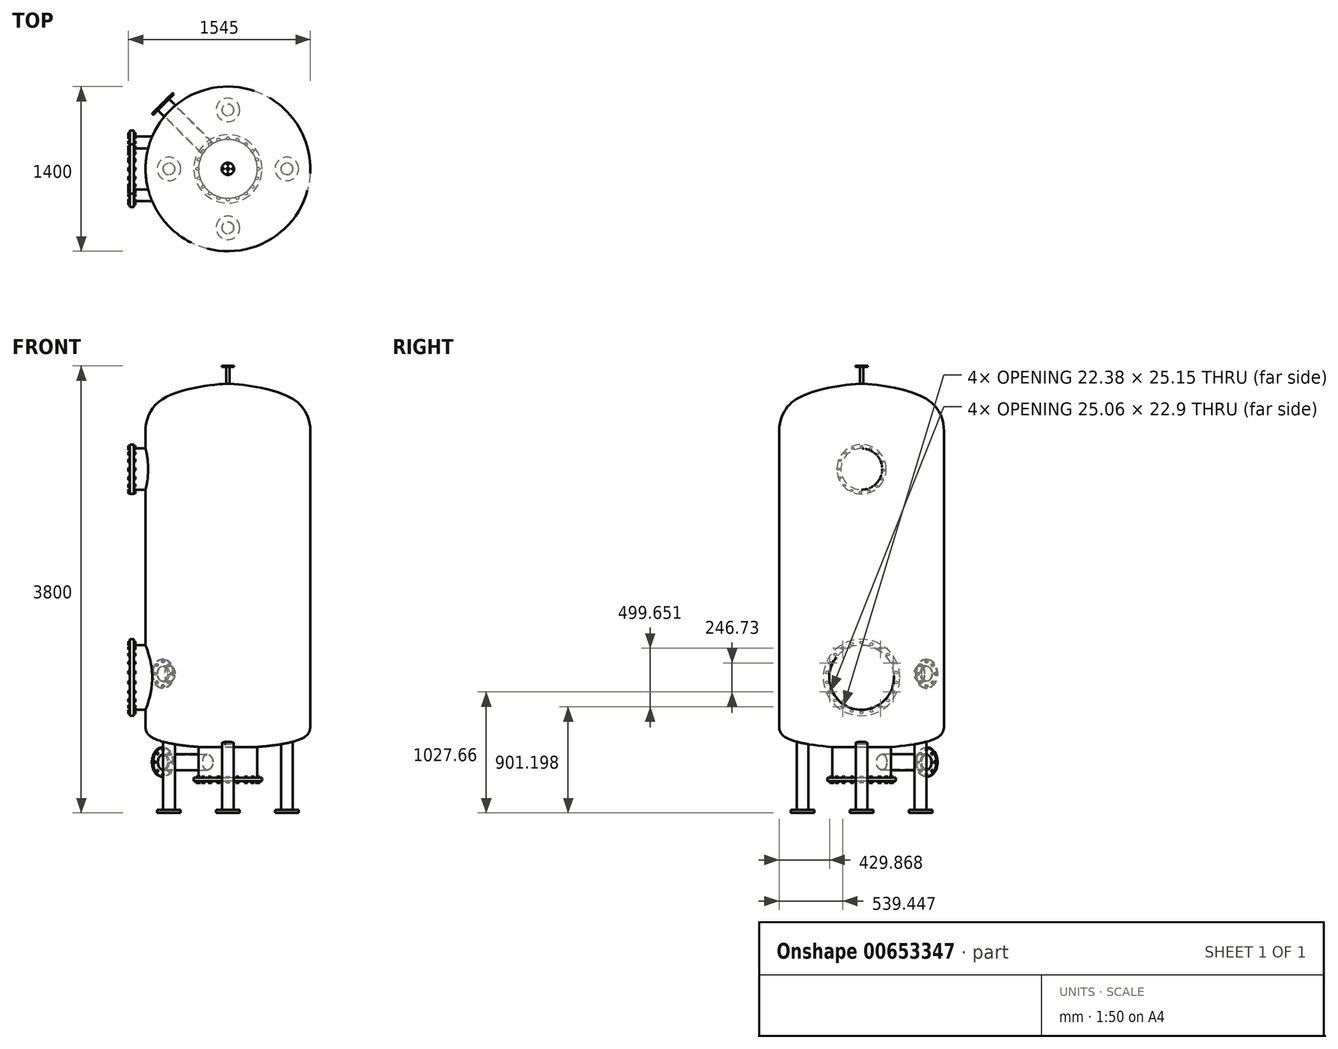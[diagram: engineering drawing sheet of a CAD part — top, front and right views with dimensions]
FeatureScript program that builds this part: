
annotation { "Feature Type Name" : "Feature", "Feature Type Description" : "" }
export const myFeature = defineFeature(function(context is Context, id is Id, definition is map)
    precondition{}
    {
        {
            var Q0;
            Q0=qCreatedBy(makeId("Front.planeOp"),FACE);
            var sketch = newSketch(context, id + "F0", { "sketchPlane" : qUnion([Q0])});
            skLineSegment(sketch, "E0.left", {"start": v(0, 0) * mm, "end": v(0, 3000) * mm});
            skLineSegment(sketch, "E0.right", {"start": v(700, 188.4) * mm, "end": v(700, 2700) * mm});
            skFitSpline(sketch, "E1", {"points": [v(700, 2700) * mm, v(561.33, 2963.36) * mm, v(0, 3098.34) * mm], "startDerivative": vector(-3.03, 549.76) * mm, "endDerivative": vector(-458.1, 7.94) * mm});
            skLineSegment(sketch, "E2", {"start": v(0, 3098.34) * mm, "end": v(0, 2986.2) * mm});
            skFitSpline(sketch, "E3", {"points": [v(0, 0) * mm, v(624.25, 80.53) * mm, v(700, 188.4) * mm], "startDerivative": vector(1247.83, 23.5) * mm, "endDerivative": vector(-2.18, 523.18) * mm});
            skSolve(sketch);
        }
        {
            var Q0;
            {var subQ1=sQuery(id+"F0.wireOp",EDGE,"E0.left");Q0=makeQuery(id+"F0.imprint","IMPRINT",FACE,{"disambiguationData":[TD([[makeQuery(id+"F0.imprint","IMPRINT",EDGE,{"derivedFrom":subQ1}),-1.0]])]});}
            var Q1;
            Q1=sQuery(id+"F0.wireOp",EDGE,"E0.left");
            revolve(context, id + "F1", {"entities" : qUnion([Q0]), "axis" : qUnion([Q1]), "revolveType" : RevolveType.FULL});
        }
        {
            var Q0;
            Q0=qCreatedBy(makeId("Top.planeOp"),FACE);
            cPlane(context, id + "F2", {"entities" : qUnion([Q0]), "cplaneType" : CPlaneType.OFFSET, "offset" : 150 * mm, "width" : 150 * mm, "height" : 150 * mm});
        }
        {
            var Q0;
            Q0=qCreatedBy(id+"F2.planeOp",FACE);
            var sketch = newSketch(context, id + "F3", { "sketchPlane" : qUnion([Q0])});
            skCircle(sketch, "E4", {"center": v(0, 0) * mm, "radius": 250 * mm});
            skSolve(sketch);
        }
        {
            var Q0;
            Q0 = qSketchRegion(id + "F3", true);
            extrude(context, id + "F4", {"entities" : qUnion([Q0]), "operationType" : NewBodyOperationType.ADD, "oppositeDirection" : true, "depth" : 400 * mm, "offsetDistance" : 25 * mm});
        }
        {
            var Q0;
            Q0=qCreatedBy(id+"F2.planeOp",FACE);
            var sketch = newSketch(context, id + "F5", { "sketchPlane" : qUnion([Q0])});
            skCircle(sketch, "E5", {"center": v(0, -500.95) * mm, "radius": 50 * mm});
            skCircle(sketch, "E6.1.0", {"center": v(500.95, 0) * mm, "radius": 50 * mm});
            skCircle(sketch, "E6.2.0", {"center": v(0, 500.95) * mm, "radius": 50 * mm});
            skCircle(sketch, "E6.3.0", {"center": v(-500.95, 0) * mm, "radius": 50 * mm});
            skPoint(sketch, "E6.center", {"position": v(0, 0) * mm});
            skSolve(sketch);
        }
        {
            var Q0;
            Q0 = qSketchRegion(id + "F5", true);
            extrude(context, id + "F6", {"entities" : qUnion([Q0]), "operationType" : NewBodyOperationType.ADD, "oppositeDirection" : true, "depth" : 700 * mm, "offsetDistance" : 25 * mm});
        }
        {
            var Q0;
            Q0=makeQuery(id+"F4.opExtrude","CAP_FACE",FACE,{"disambiguationData":[OSD([sQuery(id+"F3.wireOp",EDGE,"E4")])],"isStart":false});
            var sketch = newSketch(context, id + "F7", { "sketchPlane" : qUnion([Q0])});
            skCircle(sketch, "E7", {"center": v(0, 0) * mm, "radius": 290 * mm});
            skSolve(sketch);
        }
        {
            var Q0;
            Q0=makeQuery(id+"F7.imprint","IMPRINT",FACE,{"disambiguationData":[TD([[makeQuery(id+"F7.imprint","IMPRINT",EDGE,{"derivedFrom":sQuery(id+"F7.wireOp",EDGE,"E7")}),1.0]])]});
            var Q1;
            Q1=makeQuery(id+"F7.imprint","IMPRINT",FACE,{"disambiguationData":[TD([[makeQuery(id+"F7.imprint","IMPRINT",EDGE,{"derivedFrom":makeQuery(id+"F4.opExtrude","CAP_EDGE",EDGE,{"disambiguationData":[OSD([sQuery(id+"F3.wireOp",EDGE,"E4")])],"isStart":false})}),-1.0]])]});
            var Q2;
            Q2=sQuery(id+"F7.wireOp",EDGE,"E7");
            extrude(context, id + "F8", {"entities" : qUnion([Q0, Q1]), "operationType" : NewBodyOperationType.ADD, "surfaceEntities" : qUnion([Q2]), "depth" : 30 * mm, "offsetDistance" : 25 * mm});
        }
        {
            var Q0;
            Q0=makeQuery(id+"F8.opExtrude","CAP_FACE",FACE,{"disambiguationData":[OSD([sQuery(id+"F7.wireOp",EDGE,"E7")])],"isStart":false});
            var sketch = newSketch(context, id + "F9", { "sketchPlane" : qUnion([Q0])});
            skCircle(sketch, "E8.cCircle", {"center": v(260, 0) * mm, "radius": 12.3 * mm, "construction": true});
            skLineSegment(sketch, "E8.0", {"start": v(247.7, -7.1) * mm, "end": v(247.7, 7.1) * mm});
            skLineSegment(sketch, "E8.1", {"start": v(247.7, 7.1) * mm, "end": v(260, 14.2) * mm});
            skLineSegment(sketch, "E8.2", {"start": v(260, 14.2) * mm, "end": v(272.3, 7.1) * mm});
            skLineSegment(sketch, "E8.3", {"start": v(272.3, 7.1) * mm, "end": v(272.3, -7.1) * mm});
            skLineSegment(sketch, "E8.4", {"start": v(272.3, -7.1) * mm, "end": v(260, -14.2) * mm});
            skLineSegment(sketch, "E8.5", {"start": v(260, -14.2) * mm, "end": v(247.7, -7.1) * mm});
            skPoint(sketch, "E8.0.midPoint", {"position": v(247.7, 0) * mm});
            skLineSegment(sketch, "E9.1.0", {"start": v(242.89, 93.85) * mm, "end": v(256.78, 90.9) * mm});
            skLineSegment(sketch, "E9.1.1", {"start": v(261.17, 77.4) * mm, "end": v(251.66, 66.83) * mm});
            skLineSegment(sketch, "E9.1.2", {"start": v(251.66, 66.83) * mm, "end": v(237.77, 69.79) * mm});
            skPoint(sketch, "E9.1.3", {"position": v(235.58, 76.54) * mm});
            skCircle(sketch, "E9.1.4", {"center": v(247.27, 80.34) * mm, "radius": 12.3 * mm, "construction": true});
            skLineSegment(sketch, "E9.1.5", {"start": v(233.38, 83.3) * mm, "end": v(242.89, 93.85) * mm});
            skLineSegment(sketch, "E9.1.6", {"start": v(256.78, 90.9) * mm, "end": v(261.17, 77.4) * mm});
            skLineSegment(sketch, "E9.1.7", {"start": v(237.77, 69.79) * mm, "end": v(233.38, 83.3) * mm});
            skLineSegment(sketch, "E9.2.0", {"start": v(202, 164.32) * mm, "end": v(216.12, 165.8) * mm});
            skLineSegment(sketch, "E9.2.1", {"start": v(224.47, 154.3) * mm, "end": v(218.7, 141.33) * mm});
            skLineSegment(sketch, "E9.2.2", {"start": v(218.7, 141.33) * mm, "end": v(204.57, 139.85) * mm});
            skPoint(sketch, "E9.2.3", {"position": v(200.4, 145.6) * mm});
            skCircle(sketch, "E9.2.4", {"center": v(210.34, 152.82) * mm, "radius": 12.3 * mm, "construction": true});
            skLineSegment(sketch, "E9.2.5", {"start": v(196.22, 151.34) * mm, "end": v(202, 164.32) * mm});
            skLineSegment(sketch, "E9.2.6", {"start": v(216.12, 165.8) * mm, "end": v(224.47, 154.3) * mm});
            skLineSegment(sketch, "E9.2.7", {"start": v(204.57, 139.85) * mm, "end": v(196.22, 151.34) * mm});
            skLineSegment(sketch, "E9.3.0", {"start": v(141.33, 218.7) * mm, "end": v(154.3, 224.47) * mm});
            skLineSegment(sketch, "E9.3.1", {"start": v(165.8, 216.12) * mm, "end": v(164.32, 202) * mm});
            skLineSegment(sketch, "E9.3.2", {"start": v(164.32, 202) * mm, "end": v(151.34, 196.22) * mm});
            skPoint(sketch, "E9.3.3", {"position": v(145.6, 200.4) * mm});
            skCircle(sketch, "E9.3.4", {"center": v(152.82, 210.34) * mm, "radius": 12.3 * mm, "construction": true});
            skLineSegment(sketch, "E9.3.5", {"start": v(139.85, 204.57) * mm, "end": v(141.33, 218.7) * mm});
            skLineSegment(sketch, "E9.3.6", {"start": v(154.3, 224.47) * mm, "end": v(165.8, 216.12) * mm});
            skLineSegment(sketch, "E9.3.7", {"start": v(151.34, 196.22) * mm, "end": v(139.85, 204.57) * mm});
            skLineSegment(sketch, "E9.4.0", {"start": v(66.83, 251.66) * mm, "end": v(77.4, 261.17) * mm});
            skLineSegment(sketch, "E9.4.1", {"start": v(90.9, 256.78) * mm, "end": v(93.85, 242.89) * mm});
            skLineSegment(sketch, "E9.4.2", {"start": v(93.85, 242.89) * mm, "end": v(83.3, 233.38) * mm});
            skPoint(sketch, "E9.4.3", {"position": v(76.54, 235.58) * mm});
            skCircle(sketch, "E9.4.4", {"center": v(80.34, 247.27) * mm, "radius": 12.3 * mm, "construction": true});
            skLineSegment(sketch, "E9.4.5", {"start": v(69.79, 237.77) * mm, "end": v(66.83, 251.66) * mm});
            skLineSegment(sketch, "E9.4.6", {"start": v(77.4, 261.17) * mm, "end": v(90.9, 256.78) * mm});
            skLineSegment(sketch, "E9.4.7", {"start": v(83.3, 233.38) * mm, "end": v(69.79, 237.77) * mm});
            skLineSegment(sketch, "E9.5.0", {"start": v(-14.2, 260) * mm, "end": v(-7.1, 272.3) * mm});
            skLineSegment(sketch, "E9.5.1", {"start": v(7.1, 272.3) * mm, "end": v(14.2, 260) * mm});
            skLineSegment(sketch, "E9.5.2", {"start": v(14.2, 260) * mm, "end": v(7.1, 247.7) * mm});
            skPoint(sketch, "E9.5.3", {"position": v(0, 247.7) * mm});
            skCircle(sketch, "E9.5.4", {"center": v(0, 260) * mm, "radius": 12.3 * mm, "construction": true});
            skLineSegment(sketch, "E9.5.5", {"start": v(-7.1, 247.7) * mm, "end": v(-14.2, 260) * mm});
            skLineSegment(sketch, "E9.5.6", {"start": v(-7.1, 272.3) * mm, "end": v(7.1, 272.3) * mm});
            skLineSegment(sketch, "E9.5.7", {"start": v(7.1, 247.7) * mm, "end": v(-7.1, 247.7) * mm});
            skLineSegment(sketch, "E9.6.0", {"start": v(-93.85, 242.89) * mm, "end": v(-90.9, 256.78) * mm});
            skLineSegment(sketch, "E9.6.1", {"start": v(-77.4, 261.17) * mm, "end": v(-66.83, 251.66) * mm});
            skLineSegment(sketch, "E9.6.2", {"start": v(-66.83, 251.66) * mm, "end": v(-69.79, 237.77) * mm});
            skPoint(sketch, "E9.6.3", {"position": v(-76.54, 235.58) * mm});
            skCircle(sketch, "E9.6.4", {"center": v(-80.34, 247.27) * mm, "radius": 12.3 * mm, "construction": true});
            skLineSegment(sketch, "E9.6.5", {"start": v(-83.3, 233.38) * mm, "end": v(-93.85, 242.89) * mm});
            skLineSegment(sketch, "E9.6.6", {"start": v(-90.9, 256.78) * mm, "end": v(-77.4, 261.17) * mm});
            skLineSegment(sketch, "E9.6.7", {"start": v(-69.79, 237.77) * mm, "end": v(-83.3, 233.38) * mm});
            skLineSegment(sketch, "E9.7.0", {"start": v(-164.32, 202) * mm, "end": v(-165.8, 216.12) * mm});
            skLineSegment(sketch, "E9.7.1", {"start": v(-154.3, 224.47) * mm, "end": v(-141.33, 218.7) * mm});
            skLineSegment(sketch, "E9.7.2", {"start": v(-141.33, 218.7) * mm, "end": v(-139.85, 204.57) * mm});
            skPoint(sketch, "E9.7.3", {"position": v(-145.6, 200.4) * mm});
            skCircle(sketch, "E9.7.4", {"center": v(-152.82, 210.34) * mm, "radius": 12.3 * mm, "construction": true});
            skLineSegment(sketch, "E9.7.5", {"start": v(-151.34, 196.22) * mm, "end": v(-164.32, 202) * mm});
            skLineSegment(sketch, "E9.7.6", {"start": v(-165.8, 216.12) * mm, "end": v(-154.3, 224.47) * mm});
            skLineSegment(sketch, "E9.7.7", {"start": v(-139.85, 204.57) * mm, "end": v(-151.34, 196.22) * mm});
            skLineSegment(sketch, "E9.8.0", {"start": v(-218.7, 141.33) * mm, "end": v(-224.47, 154.3) * mm});
            skLineSegment(sketch, "E9.8.1", {"start": v(-216.12, 165.8) * mm, "end": v(-202, 164.32) * mm});
            skLineSegment(sketch, "E9.8.2", {"start": v(-202, 164.32) * mm, "end": v(-196.22, 151.34) * mm});
            skPoint(sketch, "E9.8.3", {"position": v(-200.4, 145.6) * mm});
            skCircle(sketch, "E9.8.4", {"center": v(-210.34, 152.82) * mm, "radius": 12.3 * mm, "construction": true});
            skLineSegment(sketch, "E9.8.5", {"start": v(-204.57, 139.85) * mm, "end": v(-218.7, 141.33) * mm});
            skLineSegment(sketch, "E9.8.6", {"start": v(-224.47, 154.3) * mm, "end": v(-216.12, 165.8) * mm});
            skLineSegment(sketch, "E9.8.7", {"start": v(-196.22, 151.34) * mm, "end": v(-204.57, 139.85) * mm});
            skLineSegment(sketch, "E9.9.0", {"start": v(-251.66, 66.83) * mm, "end": v(-261.17, 77.4) * mm});
            skLineSegment(sketch, "E9.9.1", {"start": v(-256.78, 90.9) * mm, "end": v(-242.89, 93.85) * mm});
            skLineSegment(sketch, "E9.9.2", {"start": v(-242.89, 93.85) * mm, "end": v(-233.38, 83.3) * mm});
            skPoint(sketch, "E9.9.3", {"position": v(-235.58, 76.54) * mm});
            skCircle(sketch, "E9.9.4", {"center": v(-247.27, 80.34) * mm, "radius": 12.3 * mm, "construction": true});
            skLineSegment(sketch, "E9.9.5", {"start": v(-237.77, 69.79) * mm, "end": v(-251.66, 66.83) * mm});
            skLineSegment(sketch, "E9.9.6", {"start": v(-261.17, 77.4) * mm, "end": v(-256.78, 90.9) * mm});
            skLineSegment(sketch, "E9.9.7", {"start": v(-233.38, 83.3) * mm, "end": v(-237.77, 69.79) * mm});
            skLineSegment(sketch, "E9.10.0", {"start": v(-260, -14.2) * mm, "end": v(-272.3, -7.1) * mm});
            skLineSegment(sketch, "E9.10.1", {"start": v(-272.3, 7.1) * mm, "end": v(-260, 14.2) * mm});
            skLineSegment(sketch, "E9.10.2", {"start": v(-260, 14.2) * mm, "end": v(-247.7, 7.1) * mm});
            skPoint(sketch, "E9.10.3", {"position": v(-247.7, 0) * mm});
            skCircle(sketch, "E9.10.4", {"center": v(-260, 0) * mm, "radius": 12.3 * mm, "construction": true});
            skLineSegment(sketch, "E9.10.5", {"start": v(-247.7, -7.1) * mm, "end": v(-260, -14.2) * mm});
            skLineSegment(sketch, "E9.10.6", {"start": v(-272.3, -7.1) * mm, "end": v(-272.3, 7.1) * mm});
            skLineSegment(sketch, "E9.10.7", {"start": v(-247.7, 7.1) * mm, "end": v(-247.7, -7.1) * mm});
            skLineSegment(sketch, "E9.11.0", {"start": v(-242.89, -93.85) * mm, "end": v(-256.78, -90.9) * mm});
            skLineSegment(sketch, "E9.11.1", {"start": v(-261.17, -77.4) * mm, "end": v(-251.66, -66.83) * mm});
            skLineSegment(sketch, "E9.11.2", {"start": v(-251.66, -66.83) * mm, "end": v(-237.77, -69.79) * mm});
            skPoint(sketch, "E9.11.3", {"position": v(-235.58, -76.54) * mm});
            skCircle(sketch, "E9.11.4", {"center": v(-247.27, -80.34) * mm, "radius": 12.3 * mm, "construction": true});
            skLineSegment(sketch, "E9.11.5", {"start": v(-233.38, -83.3) * mm, "end": v(-242.89, -93.85) * mm});
            skLineSegment(sketch, "E9.11.6", {"start": v(-256.78, -90.9) * mm, "end": v(-261.17, -77.4) * mm});
            skLineSegment(sketch, "E9.11.7", {"start": v(-237.77, -69.79) * mm, "end": v(-233.38, -83.3) * mm});
            skLineSegment(sketch, "E9.12.0", {"start": v(-202, -164.32) * mm, "end": v(-216.12, -165.8) * mm});
            skLineSegment(sketch, "E9.12.1", {"start": v(-224.47, -154.3) * mm, "end": v(-218.7, -141.33) * mm});
            skLineSegment(sketch, "E9.12.2", {"start": v(-218.7, -141.33) * mm, "end": v(-204.57, -139.85) * mm});
            skPoint(sketch, "E9.12.3", {"position": v(-200.4, -145.6) * mm});
            skCircle(sketch, "E9.12.4", {"center": v(-210.34, -152.82) * mm, "radius": 12.3 * mm, "construction": true});
            skLineSegment(sketch, "E9.12.5", {"start": v(-196.22, -151.34) * mm, "end": v(-202, -164.32) * mm});
            skLineSegment(sketch, "E9.12.6", {"start": v(-216.12, -165.8) * mm, "end": v(-224.47, -154.3) * mm});
            skLineSegment(sketch, "E9.12.7", {"start": v(-204.57, -139.85) * mm, "end": v(-196.22, -151.34) * mm});
            skLineSegment(sketch, "E9.13.0", {"start": v(-141.33, -218.7) * mm, "end": v(-154.3, -224.47) * mm});
            skLineSegment(sketch, "E9.13.1", {"start": v(-165.8, -216.12) * mm, "end": v(-164.32, -202) * mm});
            skLineSegment(sketch, "E9.13.2", {"start": v(-164.32, -202) * mm, "end": v(-151.34, -196.22) * mm});
            skPoint(sketch, "E9.13.3", {"position": v(-145.6, -200.4) * mm});
            skCircle(sketch, "E9.13.4", {"center": v(-152.82, -210.34) * mm, "radius": 12.3 * mm, "construction": true});
            skLineSegment(sketch, "E9.13.5", {"start": v(-139.85, -204.57) * mm, "end": v(-141.33, -218.7) * mm});
            skLineSegment(sketch, "E9.13.6", {"start": v(-154.3, -224.47) * mm, "end": v(-165.8, -216.12) * mm});
            skLineSegment(sketch, "E9.13.7", {"start": v(-151.34, -196.22) * mm, "end": v(-139.85, -204.57) * mm});
            skLineSegment(sketch, "E9.14.0", {"start": v(-66.83, -251.66) * mm, "end": v(-77.4, -261.17) * mm});
            skLineSegment(sketch, "E9.14.1", {"start": v(-90.9, -256.78) * mm, "end": v(-93.85, -242.89) * mm});
            skLineSegment(sketch, "E9.14.2", {"start": v(-93.85, -242.89) * mm, "end": v(-83.3, -233.38) * mm});
            skPoint(sketch, "E9.14.3", {"position": v(-76.54, -235.58) * mm});
            skCircle(sketch, "E9.14.4", {"center": v(-80.34, -247.27) * mm, "radius": 12.3 * mm, "construction": true});
            skLineSegment(sketch, "E9.14.5", {"start": v(-69.79, -237.77) * mm, "end": v(-66.83, -251.66) * mm});
            skLineSegment(sketch, "E9.14.6", {"start": v(-77.4, -261.17) * mm, "end": v(-90.9, -256.78) * mm});
            skLineSegment(sketch, "E9.14.7", {"start": v(-83.3, -233.38) * mm, "end": v(-69.79, -237.77) * mm});
            skLineSegment(sketch, "E9.15.0", {"start": v(14.2, -260) * mm, "end": v(7.1, -272.3) * mm});
            skLineSegment(sketch, "E9.15.1", {"start": v(-7.1, -272.3) * mm, "end": v(-14.2, -260) * mm});
            skLineSegment(sketch, "E9.15.2", {"start": v(-14.2, -260) * mm, "end": v(-7.1, -247.7) * mm});
            skPoint(sketch, "E9.15.3", {"position": v(0, -247.7) * mm});
            skCircle(sketch, "E9.15.4", {"center": v(0, -260) * mm, "radius": 12.3 * mm, "construction": true});
            skLineSegment(sketch, "E9.15.5", {"start": v(7.1, -247.7) * mm, "end": v(14.2, -260) * mm});
            skLineSegment(sketch, "E9.15.6", {"start": v(7.1, -272.3) * mm, "end": v(-7.1, -272.3) * mm});
            skLineSegment(sketch, "E9.15.7", {"start": v(-7.1, -247.7) * mm, "end": v(7.1, -247.7) * mm});
            skLineSegment(sketch, "E9.16.0", {"start": v(93.85, -242.89) * mm, "end": v(90.9, -256.78) * mm});
            skLineSegment(sketch, "E9.16.1", {"start": v(77.4, -261.17) * mm, "end": v(66.83, -251.66) * mm});
            skLineSegment(sketch, "E9.16.2", {"start": v(66.83, -251.66) * mm, "end": v(69.79, -237.77) * mm});
            skPoint(sketch, "E9.16.3", {"position": v(76.54, -235.58) * mm});
            skCircle(sketch, "E9.16.4", {"center": v(80.34, -247.27) * mm, "radius": 12.3 * mm, "construction": true});
            skLineSegment(sketch, "E9.16.5", {"start": v(83.3, -233.38) * mm, "end": v(93.85, -242.89) * mm});
            skLineSegment(sketch, "E9.16.6", {"start": v(90.9, -256.78) * mm, "end": v(77.4, -261.17) * mm});
            skLineSegment(sketch, "E9.16.7", {"start": v(69.79, -237.77) * mm, "end": v(83.3, -233.38) * mm});
            skLineSegment(sketch, "E9.17.0", {"start": v(164.32, -202) * mm, "end": v(165.8, -216.12) * mm});
            skLineSegment(sketch, "E9.17.1", {"start": v(154.3, -224.47) * mm, "end": v(141.33, -218.7) * mm});
            skLineSegment(sketch, "E9.17.2", {"start": v(141.33, -218.7) * mm, "end": v(139.85, -204.57) * mm});
            skPoint(sketch, "E9.17.3", {"position": v(145.6, -200.4) * mm});
            skCircle(sketch, "E9.17.4", {"center": v(152.82, -210.34) * mm, "radius": 12.3 * mm, "construction": true});
            skLineSegment(sketch, "E9.17.5", {"start": v(151.34, -196.22) * mm, "end": v(164.32, -202) * mm});
            skLineSegment(sketch, "E9.17.6", {"start": v(165.8, -216.12) * mm, "end": v(154.3, -224.47) * mm});
            skLineSegment(sketch, "E9.17.7", {"start": v(139.85, -204.57) * mm, "end": v(151.34, -196.22) * mm});
            skLineSegment(sketch, "E9.18.0", {"start": v(218.7, -141.33) * mm, "end": v(224.47, -154.3) * mm});
            skLineSegment(sketch, "E9.18.1", {"start": v(216.12, -165.8) * mm, "end": v(202, -164.32) * mm});
            skLineSegment(sketch, "E9.18.2", {"start": v(202, -164.32) * mm, "end": v(196.22, -151.34) * mm});
            skPoint(sketch, "E9.18.3", {"position": v(200.4, -145.6) * mm});
            skCircle(sketch, "E9.18.4", {"center": v(210.34, -152.82) * mm, "radius": 12.3 * mm, "construction": true});
            skLineSegment(sketch, "E9.18.5", {"start": v(204.57, -139.85) * mm, "end": v(218.7, -141.33) * mm});
            skLineSegment(sketch, "E9.18.6", {"start": v(224.47, -154.3) * mm, "end": v(216.12, -165.8) * mm});
            skLineSegment(sketch, "E9.18.7", {"start": v(196.22, -151.34) * mm, "end": v(204.57, -139.85) * mm});
            skLineSegment(sketch, "E9.19.0", {"start": v(251.66, -66.83) * mm, "end": v(261.17, -77.4) * mm});
            skLineSegment(sketch, "E9.19.1", {"start": v(256.78, -90.9) * mm, "end": v(242.89, -93.85) * mm});
            skLineSegment(sketch, "E9.19.2", {"start": v(242.89, -93.85) * mm, "end": v(233.38, -83.3) * mm});
            skPoint(sketch, "E9.19.3", {"position": v(235.58, -76.54) * mm});
            skCircle(sketch, "E9.19.4", {"center": v(247.27, -80.34) * mm, "radius": 12.3 * mm, "construction": true});
            skLineSegment(sketch, "E9.19.5", {"start": v(237.77, -69.79) * mm, "end": v(251.66, -66.83) * mm});
            skLineSegment(sketch, "E9.19.6", {"start": v(261.17, -77.4) * mm, "end": v(256.78, -90.9) * mm});
            skLineSegment(sketch, "E9.19.7", {"start": v(233.38, -83.3) * mm, "end": v(237.77, -69.79) * mm});
            skPoint(sketch, "E9.center", {"position": v(0, 0) * mm});
            skSolve(sketch);
        }
        {
            var Q0;
            Q0 = qSketchRegion(id + "F9", true);
            extrude(context, id + "F10", {"entities" : qUnion([Q0]), "operationType" : NewBodyOperationType.ADD, "depth" : 15 * mm, "offsetDistance" : 25 * mm, "hasSecondDirection" : true, "secondDirectionOppositeDirection" : true, "secondDirectionDepth" : 40 * mm});
        }
        {
            var Q0;
            Q0=makeQuery(id+"F6.opExtrude","CAP_FACE",FACE,{"disambiguationData":[OSD([sQuery(id+"F5.wireOp",EDGE,"E6.2.0")])],"isStart":false});
            var sketch = newSketch(context, id + "F11", { "sketchPlane" : qUnion([Q0])});
            skCircle(sketch, "E10", {"center": v(0, -500.95) * mm, "radius": 100 * mm});
            skCircle(sketch, "E11.1.0", {"center": v(500.95, 0) * mm, "radius": 100 * mm});
            skCircle(sketch, "E11.2.0", {"center": v(0, 500.95) * mm, "radius": 100 * mm});
            skCircle(sketch, "E11.3.0", {"center": v(-500.95, 0) * mm, "radius": 100 * mm});
            skPoint(sketch, "E11.center", {"position": v(0, 0) * mm});
            skSolve(sketch);
        }
        {
            var Q0;
            Q0 = qSketchRegion(id + "F11", true);
            extrude(context, id + "F12", {"entities" : qUnion([Q0]), "operationType" : NewBodyOperationType.ADD, "oppositeDirection" : true, "depth" : 25 * mm, "offsetDistance" : 25 * mm});
        }
        {
            var Q0;
            Q0=makeQuery(id+"F8.opExtrude","CAP_FACE",FACE,{"disambiguationData":[OSD([sQuery(id+"F7.wireOp",EDGE,"E7")])],"isStart":false});
            var sketch = newSketch(context, id + "F13", { "sketchPlane" : qUnion([Q0])});
            skLineSegment(sketch, "E12", {"start": v(0, 0) * mm, "end": v(-124.4, -124.4) * mm});
            skLineSegment(sketch, "E13", {"start": v(0, 0) * mm, "end": v(-110.44, 0) * mm});
            skSolve(sketch);
        }
        {
            var Q0;
            Q0=sQuery(id+"F13.wireOp",EDGE,"E12");
            cPlane(context, id + "F14", {"entities" : qUnion([Q0]), "cplaneType" : CPlaneType.MID_PLANE, "offset" : 25 * mm, "width" : 150 * mm, "height" : 150 * mm});
        }
        {
            var Q0;
            Q0=qCreatedBy(id+"F14.planeOp",FACE);
            var sketch = newSketch(context, id + "F15", { "sketchPlane" : qUnion([Q0])});
            skCircle(sketch, "E14", {"center": v(0, -118.9) * mm, "radius": 67.5 * mm});
            skCircle(sketch, "E15", {"center": v(0, -118.9) * mm, "radius": 62.5 * mm});
            skSolve(sketch);
        }
        {
            var Q0;
            Q0 = qSketchRegion(id + "F15", true);
            extrude(context, id + "F16", {"entities" : qUnion([Q0]), "operationType" : NewBodyOperationType.ADD, "depth" : 700 * mm, "offsetDistance" : 25 * mm});
        }
        {
            var Q0;
            Q0=makeQuery(id+"F16.opExtrude","CAP_FACE",FACE,{"disambiguationData":[OSD([sQuery(id+"F15.wireOp",EDGE,"E14"),sQuery(id+"F15.wireOp",EDGE,"E15")])],"isStart":false});
            var sketch = newSketch(context, id + "F17", { "sketchPlane" : qUnion([Q0])});
            skCircle(sketch, "E16", {"center": v(0, -118.9) * mm, "radius": 125 * mm});
            skCircle(sketch, "E17", {"center": v(0, -13.9) * mm, "radius": 9 * mm});
            skCircle(sketch, "E18.1.0", {"center": v(-74.25, -44.65) * mm, "radius": 9 * mm});
            skCircle(sketch, "E18.2.0", {"center": v(-105, -118.9) * mm, "radius": 9 * mm});
            skCircle(sketch, "E18.3.0", {"center": v(-74.25, -193.14) * mm, "radius": 9 * mm});
            skCircle(sketch, "E18.4.0", {"center": v(0, -223.9) * mm, "radius": 9 * mm});
            skCircle(sketch, "E18.5.0", {"center": v(74.25, -193.14) * mm, "radius": 9 * mm});
            skCircle(sketch, "E18.6.0", {"center": v(105, -118.9) * mm, "radius": 9 * mm});
            skCircle(sketch, "E18.7.0", {"center": v(74.25, -44.65) * mm, "radius": 9 * mm});
            skSolve(sketch);
        }
        {
            var Q0;
            Q0=makeQuery(id+"F17.imprint","IMPRINT",FACE,{"disambiguationData":[TD([[makeQuery(id+"F17.imprint","IMPRINT",EDGE,{"derivedFrom":sQuery(id+"F17.wireOp",EDGE,"E16")}),1.0]])]});
            extrude(context, id + "F18", {"entities" : qUnion([Q0]), "operationType" : NewBodyOperationType.ADD, "oppositeDirection" : true, "depth" : 15 * mm, "offsetDistance" : 25 * mm});
        }
        {
            var Q0;
            Q0=qCreatedBy(makeId("Right.planeOp"),FACE);
            var sketch = newSketch(context, id + "F19", { "sketchPlane" : qUnion([Q0])});
            skCircle(sketch, "E19", {"center": v(0, 2372.8) * mm, "radius": 175 * mm});
            skCircle(sketch, "E20", {"center": v(0, 601.02) * mm, "radius": 275 * mm});
            skSolve(sketch);
        }
        {
            var Q0;
            Q0 = qSketchRegion(id + "F19", true);
            extrude(context, id + "F20", {"entities" : qUnion([Q0]), "operationType" : NewBodyOperationType.ADD, "oppositeDirection" : true, "depth" : 800 * mm, "offsetDistance" : 25 * mm});
        }
        {
            var Q0;
            Q0=makeQuery(id+"F20.opExtrude","CAP_FACE",FACE,{"disambiguationData":[OSD([sQuery(id+"F19.wireOp",EDGE,"E20")])],"isStart":false});
            var sketch = newSketch(context, id + "F21", { "sketchPlane" : qUnion([Q0])});
            skCircle(sketch, "E21", {"center": v(0, 601.02) * mm, "radius": 325 * mm});
            skCircle(sketch, "E22", {"center": v(0, 2372.16) * mm, "radius": 210 * mm});
            skSolve(sketch);
        }
        {
            var Q0;
            Q0 = qSketchRegion(id + "F21", true);
            extrude(context, id + "F22", {"entities" : qUnion([Q0]), "operationType" : NewBodyOperationType.ADD, "depth" : 35 * mm, "offsetDistance" : 25 * mm});
        }
        {
            var Q0;
            Q0=makeQuery(id+"F22.opExtrude","CAP_FACE",FACE,{"disambiguationData":[OSD([sQuery(id+"F21.wireOp",EDGE,"E21")])],"isStart":false});
            var sketch = newSketch(context, id + "F23", { "sketchPlane" : qUnion([Q0])});
            skCircle(sketch, "E23.cCircle", {"center": v(0, 898) * mm, "radius": 10.9 * mm, "construction": true});
            skLineSegment(sketch, "E23.0", {"start": v(6.3, 887.09) * mm, "end": v(-6.3, 887.09) * mm});
            skLineSegment(sketch, "E23.1", {"start": v(-6.3, 887.09) * mm, "end": v(-12.59, 898) * mm});
            skLineSegment(sketch, "E23.2", {"start": v(-12.59, 898) * mm, "end": v(-6.3, 908.9) * mm});
            skLineSegment(sketch, "E23.3", {"start": v(-6.3, 908.9) * mm, "end": v(6.3, 908.9) * mm});
            skLineSegment(sketch, "E23.4", {"start": v(6.3, 908.9) * mm, "end": v(12.59, 898) * mm});
            skLineSegment(sketch, "E23.5", {"start": v(12.59, 898) * mm, "end": v(6.3, 887.09) * mm});
            skPoint(sketch, "E23.0.midPoint", {"position": v(0, 887.09) * mm});
            skLineSegment(sketch, "E24.1.0", {"start": v(-86.63, 873.73) * mm, "end": v(-95.75, 882.42) * mm});
            skCircle(sketch, "E24.1.1", {"center": v(-83.67, 885.96) * mm, "radius": 10.9 * mm, "construction": true});
            skPoint(sketch, "E24.1.2", {"position": v(-80.6, 875.5) * mm});
            skLineSegment(sketch, "E24.1.3", {"start": v(-71.59, 889.5) * mm, "end": v(-74.55, 877.28) * mm});
            skLineSegment(sketch, "E24.1.4", {"start": v(-92.78, 894.65) * mm, "end": v(-80.7, 898.2) * mm});
            skLineSegment(sketch, "E24.1.5", {"start": v(-74.55, 877.28) * mm, "end": v(-86.63, 873.73) * mm});
            skLineSegment(sketch, "E24.1.6", {"start": v(-80.7, 898.2) * mm, "end": v(-71.59, 889.5) * mm});
            skLineSegment(sketch, "E24.1.7", {"start": v(-95.75, 882.42) * mm, "end": v(-92.78, 894.65) * mm});
            skLineSegment(sketch, "E24.2.0", {"start": v(-159.95, 838.27) * mm, "end": v(-171.14, 844.04) * mm});
            skCircle(sketch, "E24.2.1", {"center": v(-160.55, 850.85) * mm, "radius": 10.9 * mm, "construction": true});
            skPoint(sketch, "E24.2.2", {"position": v(-154.66, 841.68) * mm});
            skLineSegment(sketch, "E24.2.3", {"start": v(-149.96, 857.66) * mm, "end": v(-149.36, 845.08) * mm});
            skLineSegment(sketch, "E24.2.4", {"start": v(-171.74, 856.62) * mm, "end": v(-161.15, 863.42) * mm});
            skLineSegment(sketch, "E24.2.5", {"start": v(-149.36, 845.08) * mm, "end": v(-159.95, 838.27) * mm});
            skLineSegment(sketch, "E24.2.6", {"start": v(-161.15, 863.42) * mm, "end": v(-149.96, 857.66) * mm});
            skLineSegment(sketch, "E24.2.7", {"start": v(-171.14, 844.04) * mm, "end": v(-171.74, 856.62) * mm});
            skLineSegment(sketch, "E24.3.0", {"start": v(-220.32, 783.6) * mm, "end": v(-232.68, 785.98) * mm});
            skCircle(sketch, "E24.3.1", {"center": v(-224.43, 795.5) * mm, "radius": 10.9 * mm, "construction": true});
            skPoint(sketch, "E24.3.2", {"position": v(-216.2, 788.36) * mm});
            skLineSegment(sketch, "E24.3.3", {"start": v(-216.19, 805.01) * mm, "end": v(-212.07, 793.11) * mm});
            skLineSegment(sketch, "E24.3.4", {"start": v(-236.8, 797.88) * mm, "end": v(-228.55, 807.4) * mm});
            skLineSegment(sketch, "E24.3.5", {"start": v(-212.07, 793.11) * mm, "end": v(-220.32, 783.6) * mm});
            skLineSegment(sketch, "E24.3.6", {"start": v(-228.55, 807.4) * mm, "end": v(-216.19, 805.01) * mm});
            skLineSegment(sketch, "E24.3.7", {"start": v(-232.68, 785.98) * mm, "end": v(-236.8, 797.88) * mm});
            skLineSegment(sketch, "E24.4.0", {"start": v(-262.83, 714.13) * mm, "end": v(-275.36, 712.94) * mm});
            skCircle(sketch, "E24.4.1", {"center": v(-270.13, 724.39) * mm, "radius": 10.9 * mm, "construction": true});
            skPoint(sketch, "E24.4.2", {"position": v(-260.21, 719.86) * mm});
            skLineSegment(sketch, "E24.4.3", {"start": v(-264.9, 735.84) * mm, "end": v(-257.6, 725.59) * mm});
            skLineSegment(sketch, "E24.4.4", {"start": v(-282.66, 723.2) * mm, "end": v(-277.43, 734.64) * mm});
            skLineSegment(sketch, "E24.4.5", {"start": v(-257.6, 725.59) * mm, "end": v(-262.83, 714.13) * mm});
            skLineSegment(sketch, "E24.4.6", {"start": v(-277.43, 734.64) * mm, "end": v(-264.9, 735.84) * mm});
            skLineSegment(sketch, "E24.4.7", {"start": v(-275.36, 712.94) * mm, "end": v(-282.66, 723.2) * mm});
            skLineSegment(sketch, "E24.5.0", {"start": v(-284.05, 635.5) * mm, "end": v(-295.74, 630.83) * mm});
            skCircle(sketch, "E24.5.1", {"center": v(-293.95, 643.29) * mm, "radius": 10.9 * mm, "construction": true});
            skPoint(sketch, "E24.5.2", {"position": v(-283.15, 641.74) * mm});
            skLineSegment(sketch, "E24.5.3", {"start": v(-292.15, 655.75) * mm, "end": v(-282.26, 647.97) * mm});
            skLineSegment(sketch, "E24.5.4", {"start": v(-305.63, 638.6) * mm, "end": v(-303.84, 651.07) * mm});
            skLineSegment(sketch, "E24.5.5", {"start": v(-282.26, 647.97) * mm, "end": v(-284.05, 635.5) * mm});
            skLineSegment(sketch, "E24.5.6", {"start": v(-303.84, 651.07) * mm, "end": v(-292.15, 655.75) * mm});
            skLineSegment(sketch, "E24.5.7", {"start": v(-295.74, 630.83) * mm, "end": v(-305.63, 638.6) * mm});
            skLineSegment(sketch, "E24.6.0", {"start": v(-282.26, 554.08) * mm, "end": v(-292.15, 546.3) * mm});
            skCircle(sketch, "E24.6.1", {"center": v(-293.95, 558.76) * mm, "radius": 10.9 * mm, "construction": true});
            skPoint(sketch, "E24.6.2", {"position": v(-283.15, 560.31) * mm});
            skLineSegment(sketch, "E24.6.3", {"start": v(-295.74, 571.22) * mm, "end": v(-284.05, 566.54) * mm});
            skLineSegment(sketch, "E24.6.4", {"start": v(-303.84, 550.98) * mm, "end": v(-305.63, 563.44) * mm});
            skLineSegment(sketch, "E24.6.5", {"start": v(-284.05, 566.54) * mm, "end": v(-282.26, 554.08) * mm});
            skLineSegment(sketch, "E24.6.6", {"start": v(-305.63, 563.44) * mm, "end": v(-295.74, 571.22) * mm});
            skLineSegment(sketch, "E24.6.7", {"start": v(-292.15, 546.3) * mm, "end": v(-303.84, 550.98) * mm});
            skLineSegment(sketch, "E24.7.0", {"start": v(-257.6, 476.46) * mm, "end": v(-264.9, 466.2) * mm});
            skCircle(sketch, "E24.7.1", {"center": v(-270.13, 477.66) * mm, "radius": 10.9 * mm, "construction": true});
            skPoint(sketch, "E24.7.2", {"position": v(-260.21, 482.19) * mm});
            skLineSegment(sketch, "E24.7.3", {"start": v(-275.36, 489.11) * mm, "end": v(-262.83, 487.91) * mm});
            skLineSegment(sketch, "E24.7.4", {"start": v(-277.43, 467.4) * mm, "end": v(-282.66, 478.86) * mm});
            skLineSegment(sketch, "E24.7.5", {"start": v(-262.83, 487.91) * mm, "end": v(-257.6, 476.46) * mm});
            skLineSegment(sketch, "E24.7.6", {"start": v(-282.66, 478.86) * mm, "end": v(-275.36, 489.11) * mm});
            skLineSegment(sketch, "E24.7.7", {"start": v(-264.9, 466.2) * mm, "end": v(-277.43, 467.4) * mm});
            skLineSegment(sketch, "E24.8.0", {"start": v(-212.07, 408.93) * mm, "end": v(-216.19, 397.04) * mm});
            skCircle(sketch, "E24.8.1", {"center": v(-224.43, 406.55) * mm, "radius": 10.9 * mm, "construction": true});
            skPoint(sketch, "E24.8.2", {"position": v(-216.2, 413.7) * mm});
            skLineSegment(sketch, "E24.8.3", {"start": v(-232.68, 416.07) * mm, "end": v(-220.32, 418.45) * mm});
            skLineSegment(sketch, "E24.8.4", {"start": v(-228.55, 394.65) * mm, "end": v(-236.8, 404.17) * mm});
            skLineSegment(sketch, "E24.8.5", {"start": v(-220.32, 418.45) * mm, "end": v(-212.07, 408.93) * mm});
            skLineSegment(sketch, "E24.8.6", {"start": v(-236.8, 404.17) * mm, "end": v(-232.68, 416.07) * mm});
            skLineSegment(sketch, "E24.8.7", {"start": v(-216.19, 397.04) * mm, "end": v(-228.55, 394.65) * mm});
            skLineSegment(sketch, "E24.9.0", {"start": v(-149.36, 356.97) * mm, "end": v(-149.96, 344.4) * mm});
            skCircle(sketch, "E24.9.1", {"center": v(-160.55, 351.2) * mm, "radius": 10.9 * mm, "construction": true});
            skPoint(sketch, "E24.9.2", {"position": v(-154.66, 360.37) * mm});
            skLineSegment(sketch, "E24.9.3", {"start": v(-171.14, 358) * mm, "end": v(-159.95, 363.77) * mm});
            skLineSegment(sketch, "E24.9.4", {"start": v(-161.15, 338.62) * mm, "end": v(-171.74, 345.43) * mm});
            skLineSegment(sketch, "E24.9.5", {"start": v(-159.95, 363.77) * mm, "end": v(-149.36, 356.97) * mm});
            skLineSegment(sketch, "E24.9.6", {"start": v(-171.74, 345.43) * mm, "end": v(-171.14, 358) * mm});
            skLineSegment(sketch, "E24.9.7", {"start": v(-149.96, 344.4) * mm, "end": v(-161.15, 338.62) * mm});
            skLineSegment(sketch, "E24.10.0", {"start": v(-74.55, 324.77) * mm, "end": v(-71.59, 312.54) * mm});
            skCircle(sketch, "E24.10.1", {"center": v(-83.67, 316.08) * mm, "radius": 10.9 * mm, "construction": true});
            skPoint(sketch, "E24.10.2", {"position": v(-80.6, 326.55) * mm});
            skLineSegment(sketch, "E24.10.3", {"start": v(-95.75, 319.63) * mm, "end": v(-86.63, 328.32) * mm});
            skLineSegment(sketch, "E24.10.4", {"start": v(-80.7, 303.85) * mm, "end": v(-92.78, 307.4) * mm});
            skLineSegment(sketch, "E24.10.5", {"start": v(-86.63, 328.32) * mm, "end": v(-74.55, 324.77) * mm});
            skLineSegment(sketch, "E24.10.6", {"start": v(-92.78, 307.4) * mm, "end": v(-95.75, 319.63) * mm});
            skLineSegment(sketch, "E24.10.7", {"start": v(-71.59, 312.54) * mm, "end": v(-80.7, 303.85) * mm});
            skLineSegment(sketch, "E24.11.0", {"start": v(6.3, 314.96) * mm, "end": v(12.59, 304.06) * mm});
            skCircle(sketch, "E24.11.1", {"center": v(0, 304.06) * mm, "radius": 10.9 * mm, "construction": true});
            skPoint(sketch, "E24.11.2", {"position": v(0, 314.96) * mm});
            skLineSegment(sketch, "E24.11.3", {"start": v(-12.59, 304.06) * mm, "end": v(-6.3, 314.96) * mm});
            skLineSegment(sketch, "E24.11.4", {"start": v(6.3, 293.15) * mm, "end": v(-6.3, 293.15) * mm});
            skLineSegment(sketch, "E24.11.5", {"start": v(-6.3, 314.96) * mm, "end": v(6.3, 314.96) * mm});
            skLineSegment(sketch, "E24.11.6", {"start": v(-6.3, 293.15) * mm, "end": v(-12.59, 304.06) * mm});
            skLineSegment(sketch, "E24.11.7", {"start": v(12.59, 304.06) * mm, "end": v(6.3, 293.15) * mm});
            skLineSegment(sketch, "E24.12.0", {"start": v(86.63, 328.32) * mm, "end": v(95.75, 319.63) * mm});
            skCircle(sketch, "E24.12.1", {"center": v(83.67, 316.08) * mm, "radius": 10.9 * mm, "construction": true});
            skPoint(sketch, "E24.12.2", {"position": v(80.6, 326.55) * mm});
            skLineSegment(sketch, "E24.12.3", {"start": v(71.59, 312.54) * mm, "end": v(74.55, 324.77) * mm});
            skLineSegment(sketch, "E24.12.4", {"start": v(92.78, 307.4) * mm, "end": v(80.7, 303.85) * mm});
            skLineSegment(sketch, "E24.12.5", {"start": v(74.55, 324.77) * mm, "end": v(86.63, 328.32) * mm});
            skLineSegment(sketch, "E24.12.6", {"start": v(80.7, 303.85) * mm, "end": v(71.59, 312.54) * mm});
            skLineSegment(sketch, "E24.12.7", {"start": v(95.75, 319.63) * mm, "end": v(92.78, 307.4) * mm});
            skLineSegment(sketch, "E24.13.0", {"start": v(159.95, 363.77) * mm, "end": v(171.14, 358) * mm});
            skCircle(sketch, "E24.13.1", {"center": v(160.55, 351.2) * mm, "radius": 10.9 * mm, "construction": true});
            skPoint(sketch, "E24.13.2", {"position": v(154.66, 360.37) * mm});
            skLineSegment(sketch, "E24.13.3", {"start": v(149.96, 344.4) * mm, "end": v(149.36, 356.97) * mm});
            skLineSegment(sketch, "E24.13.4", {"start": v(171.74, 345.43) * mm, "end": v(161.15, 338.62) * mm});
            skLineSegment(sketch, "E24.13.5", {"start": v(149.36, 356.97) * mm, "end": v(159.95, 363.77) * mm});
            skLineSegment(sketch, "E24.13.6", {"start": v(161.15, 338.62) * mm, "end": v(149.96, 344.4) * mm});
            skLineSegment(sketch, "E24.13.7", {"start": v(171.14, 358) * mm, "end": v(171.74, 345.43) * mm});
            skLineSegment(sketch, "E24.14.0", {"start": v(220.32, 418.45) * mm, "end": v(232.68, 416.07) * mm});
            skCircle(sketch, "E24.14.1", {"center": v(224.43, 406.55) * mm, "radius": 10.9 * mm, "construction": true});
            skPoint(sketch, "E24.14.2", {"position": v(216.2, 413.7) * mm});
            skLineSegment(sketch, "E24.14.3", {"start": v(216.19, 397.04) * mm, "end": v(212.07, 408.93) * mm});
            skLineSegment(sketch, "E24.14.4", {"start": v(236.8, 404.17) * mm, "end": v(228.55, 394.65) * mm});
            skLineSegment(sketch, "E24.14.5", {"start": v(212.07, 408.93) * mm, "end": v(220.32, 418.45) * mm});
            skLineSegment(sketch, "E24.14.6", {"start": v(228.55, 394.65) * mm, "end": v(216.19, 397.04) * mm});
            skLineSegment(sketch, "E24.14.7", {"start": v(232.68, 416.07) * mm, "end": v(236.8, 404.17) * mm});
            skLineSegment(sketch, "E24.15.0", {"start": v(262.83, 487.91) * mm, "end": v(275.36, 489.11) * mm});
            skCircle(sketch, "E24.15.1", {"center": v(270.13, 477.66) * mm, "radius": 10.9 * mm, "construction": true});
            skPoint(sketch, "E24.15.2", {"position": v(260.21, 482.19) * mm});
            skLineSegment(sketch, "E24.15.3", {"start": v(264.9, 466.2) * mm, "end": v(257.6, 476.46) * mm});
            skLineSegment(sketch, "E24.15.4", {"start": v(282.66, 478.86) * mm, "end": v(277.43, 467.4) * mm});
            skLineSegment(sketch, "E24.15.5", {"start": v(257.6, 476.46) * mm, "end": v(262.83, 487.91) * mm});
            skLineSegment(sketch, "E24.15.6", {"start": v(277.43, 467.4) * mm, "end": v(264.9, 466.2) * mm});
            skLineSegment(sketch, "E24.15.7", {"start": v(275.36, 489.11) * mm, "end": v(282.66, 478.86) * mm});
            skLineSegment(sketch, "E24.16.0", {"start": v(284.05, 566.54) * mm, "end": v(295.74, 571.22) * mm});
            skCircle(sketch, "E24.16.1", {"center": v(293.95, 558.76) * mm, "radius": 10.9 * mm, "construction": true});
            skPoint(sketch, "E24.16.2", {"position": v(283.15, 560.31) * mm});
            skLineSegment(sketch, "E24.16.3", {"start": v(292.15, 546.3) * mm, "end": v(282.26, 554.08) * mm});
            skLineSegment(sketch, "E24.16.4", {"start": v(305.63, 563.44) * mm, "end": v(303.84, 550.98) * mm});
            skLineSegment(sketch, "E24.16.5", {"start": v(282.26, 554.08) * mm, "end": v(284.05, 566.54) * mm});
            skLineSegment(sketch, "E24.16.6", {"start": v(303.84, 550.98) * mm, "end": v(292.15, 546.3) * mm});
            skLineSegment(sketch, "E24.16.7", {"start": v(295.74, 571.22) * mm, "end": v(305.63, 563.44) * mm});
            skLineSegment(sketch, "E24.17.0", {"start": v(282.26, 647.97) * mm, "end": v(292.15, 655.75) * mm});
            skCircle(sketch, "E24.17.1", {"center": v(293.95, 643.29) * mm, "radius": 10.9 * mm, "construction": true});
            skPoint(sketch, "E24.17.2", {"position": v(283.15, 641.74) * mm});
            skLineSegment(sketch, "E24.17.3", {"start": v(295.74, 630.83) * mm, "end": v(284.05, 635.5) * mm});
            skLineSegment(sketch, "E24.17.4", {"start": v(303.84, 651.07) * mm, "end": v(305.63, 638.6) * mm});
            skLineSegment(sketch, "E24.17.5", {"start": v(284.05, 635.5) * mm, "end": v(282.26, 647.97) * mm});
            skLineSegment(sketch, "E24.17.6", {"start": v(305.63, 638.6) * mm, "end": v(295.74, 630.83) * mm});
            skLineSegment(sketch, "E24.17.7", {"start": v(292.15, 655.75) * mm, "end": v(303.84, 651.07) * mm});
            skLineSegment(sketch, "E24.18.0", {"start": v(257.6, 725.59) * mm, "end": v(264.9, 735.84) * mm});
            skCircle(sketch, "E24.18.1", {"center": v(270.13, 724.39) * mm, "radius": 10.9 * mm, "construction": true});
            skPoint(sketch, "E24.18.2", {"position": v(260.21, 719.86) * mm});
            skLineSegment(sketch, "E24.18.3", {"start": v(275.36, 712.94) * mm, "end": v(262.83, 714.13) * mm});
            skLineSegment(sketch, "E24.18.4", {"start": v(277.43, 734.64) * mm, "end": v(282.66, 723.2) * mm});
            skLineSegment(sketch, "E24.18.5", {"start": v(262.83, 714.13) * mm, "end": v(257.6, 725.59) * mm});
            skLineSegment(sketch, "E24.18.6", {"start": v(282.66, 723.2) * mm, "end": v(275.36, 712.94) * mm});
            skLineSegment(sketch, "E24.18.7", {"start": v(264.9, 735.84) * mm, "end": v(277.43, 734.64) * mm});
            skLineSegment(sketch, "E24.19.0", {"start": v(212.07, 793.11) * mm, "end": v(216.19, 805.01) * mm});
            skCircle(sketch, "E24.19.1", {"center": v(224.43, 795.5) * mm, "radius": 10.9 * mm, "construction": true});
            skPoint(sketch, "E24.19.2", {"position": v(216.2, 788.36) * mm});
            skLineSegment(sketch, "E24.19.3", {"start": v(232.68, 785.98) * mm, "end": v(220.32, 783.6) * mm});
            skLineSegment(sketch, "E24.19.4", {"start": v(228.55, 807.4) * mm, "end": v(236.8, 797.88) * mm});
            skLineSegment(sketch, "E24.19.5", {"start": v(220.32, 783.6) * mm, "end": v(212.07, 793.11) * mm});
            skLineSegment(sketch, "E24.19.6", {"start": v(236.8, 797.88) * mm, "end": v(232.68, 785.98) * mm});
            skLineSegment(sketch, "E24.19.7", {"start": v(216.19, 805.01) * mm, "end": v(228.55, 807.4) * mm});
            skLineSegment(sketch, "E24.20.0", {"start": v(149.36, 845.08) * mm, "end": v(149.96, 857.66) * mm});
            skCircle(sketch, "E24.20.1", {"center": v(160.55, 850.85) * mm, "radius": 10.9 * mm, "construction": true});
            skPoint(sketch, "E24.20.2", {"position": v(154.66, 841.68) * mm});
            skLineSegment(sketch, "E24.20.3", {"start": v(171.14, 844.04) * mm, "end": v(159.95, 838.27) * mm});
            skLineSegment(sketch, "E24.20.4", {"start": v(161.15, 863.42) * mm, "end": v(171.74, 856.62) * mm});
            skLineSegment(sketch, "E24.20.5", {"start": v(159.95, 838.27) * mm, "end": v(149.36, 845.08) * mm});
            skLineSegment(sketch, "E24.20.6", {"start": v(171.74, 856.62) * mm, "end": v(171.14, 844.04) * mm});
            skLineSegment(sketch, "E24.20.7", {"start": v(149.96, 857.66) * mm, "end": v(161.15, 863.42) * mm});
            skLineSegment(sketch, "E24.21.0", {"start": v(74.55, 877.28) * mm, "end": v(71.59, 889.5) * mm});
            skCircle(sketch, "E24.21.1", {"center": v(83.67, 885.96) * mm, "radius": 10.9 * mm, "construction": true});
            skPoint(sketch, "E24.21.2", {"position": v(80.6, 875.5) * mm});
            skLineSegment(sketch, "E24.21.3", {"start": v(95.75, 882.42) * mm, "end": v(86.63, 873.73) * mm});
            skLineSegment(sketch, "E24.21.4", {"start": v(80.7, 898.2) * mm, "end": v(92.78, 894.65) * mm});
            skLineSegment(sketch, "E24.21.5", {"start": v(86.63, 873.73) * mm, "end": v(74.55, 877.28) * mm});
            skLineSegment(sketch, "E24.21.6", {"start": v(92.78, 894.65) * mm, "end": v(95.75, 882.42) * mm});
            skLineSegment(sketch, "E24.21.7", {"start": v(71.59, 889.5) * mm, "end": v(80.7, 898.2) * mm});
            skPoint(sketch, "E24.center", {"position": v(0, 601.02) * mm});
            skCircle(sketch, "E25.cCircle", {"center": v(0, 2561.74) * mm, "radius": 9.07 * mm, "construction": true});
            skLineSegment(sketch, "E25.0", {"start": v(5.24, 2552.67) * mm, "end": v(-5.24, 2552.67) * mm});
            skLineSegment(sketch, "E25.1", {"start": v(-5.24, 2552.67) * mm, "end": v(-10.47, 2561.74) * mm});
            skLineSegment(sketch, "E25.2", {"start": v(-10.47, 2561.74) * mm, "end": v(-5.24, 2570.81) * mm});
            skLineSegment(sketch, "E25.3", {"start": v(-5.24, 2570.81) * mm, "end": v(5.24, 2570.81) * mm});
            skLineSegment(sketch, "E25.4", {"start": v(5.24, 2570.81) * mm, "end": v(10.47, 2561.74) * mm});
            skLineSegment(sketch, "E25.5", {"start": v(10.47, 2561.74) * mm, "end": v(5.24, 2552.67) * mm});
            skPoint(sketch, "E25.0.midPoint", {"position": v(0, 2552.67) * mm});
            skLineSegment(sketch, "E26.1.0", {"start": v(-72.38, 2555.37) * mm, "end": v(-64.07, 2549) * mm});
            skLineSegment(sketch, "E26.1.1", {"start": v(-75.11, 2534.6) * mm, "end": v(-83.42, 2540.98) * mm});
            skLineSegment(sketch, "E26.1.2", {"start": v(-82.05, 2551.37) * mm, "end": v(-72.38, 2555.37) * mm});
            skLineSegment(sketch, "E26.1.3", {"start": v(-83.42, 2540.98) * mm, "end": v(-82.05, 2551.37) * mm});
            skCircle(sketch, "E26.1.4", {"center": v(-73.74, 2545) * mm, "radius": 9.07 * mm, "construction": true});
            skPoint(sketch, "E26.1.5", {"position": v(-70.27, 2536.61) * mm});
            skLineSegment(sketch, "E26.1.6", {"start": v(-64.07, 2549) * mm, "end": v(-65.43, 2538.61) * mm});
            skLineSegment(sketch, "E26.1.7", {"start": v(-65.43, 2538.61) * mm, "end": v(-75.11, 2534.6) * mm});
            skLineSegment(sketch, "E26.2.0", {"start": v(-138.17, 2511.41) * mm, "end": v(-128.06, 2508.7) * mm});
            skLineSegment(sketch, "E26.2.1", {"start": v(-132.75, 2491.18) * mm, "end": v(-142.87, 2493.89) * mm});
            skLineSegment(sketch, "E26.2.2", {"start": v(-145.58, 2504) * mm, "end": v(-138.17, 2511.41) * mm});
            skLineSegment(sketch, "E26.2.3", {"start": v(-142.87, 2493.89) * mm, "end": v(-145.58, 2504) * mm});
            skCircle(sketch, "E26.2.4", {"center": v(-135.46, 2501.3) * mm, "radius": 9.07 * mm, "construction": true});
            skPoint(sketch, "E26.2.5", {"position": v(-129.05, 2494.88) * mm});
            skLineSegment(sketch, "E26.2.6", {"start": v(-128.06, 2508.7) * mm, "end": v(-125.35, 2498.58) * mm});
            skLineSegment(sketch, "E26.2.7", {"start": v(-125.35, 2498.58) * mm, "end": v(-132.75, 2491.18) * mm});
            skLineSegment(sketch, "E26.3.0", {"start": v(-182.14, 2445.61) * mm, "end": v(-171.75, 2446.98) * mm});
            skLineSegment(sketch, "E26.3.1", {"start": v(-169.39, 2429) * mm, "end": v(-179.77, 2427.63) * mm});
            skLineSegment(sketch, "E26.3.2", {"start": v(-186.15, 2435.94) * mm, "end": v(-182.14, 2445.61) * mm});
            skLineSegment(sketch, "E26.3.3", {"start": v(-179.77, 2427.63) * mm, "end": v(-186.15, 2435.94) * mm});
            skCircle(sketch, "E26.3.4", {"center": v(-175.76, 2437.3) * mm, "radius": 9.07 * mm, "construction": true});
            skPoint(sketch, "E26.3.5", {"position": v(-167.38, 2433.83) * mm});
            skLineSegment(sketch, "E26.3.6", {"start": v(-171.75, 2446.98) * mm, "end": v(-165.38, 2438.67) * mm});
            skLineSegment(sketch, "E26.3.7", {"start": v(-165.38, 2438.67) * mm, "end": v(-169.39, 2429) * mm});
            skLineSegment(sketch, "E26.4.0", {"start": v(-197.58, 2368) * mm, "end": v(-188.5, 2373.24) * mm});
            skLineSegment(sketch, "E26.4.1", {"start": v(-179.44, 2357.53) * mm, "end": v(-188.5, 2352.29) * mm});
            skLineSegment(sketch, "E26.4.2", {"start": v(-197.58, 2357.53) * mm, "end": v(-197.58, 2368) * mm});
            skLineSegment(sketch, "E26.4.3", {"start": v(-188.5, 2352.29) * mm, "end": v(-197.58, 2357.53) * mm});
            skCircle(sketch, "E26.4.4", {"center": v(-188.5, 2362.76) * mm, "radius": 9.07 * mm, "construction": true});
            skPoint(sketch, "E26.4.5", {"position": v(-179.44, 2362.76) * mm});
            skLineSegment(sketch, "E26.4.6", {"start": v(-188.5, 2373.24) * mm, "end": v(-179.44, 2368) * mm});
            skLineSegment(sketch, "E26.4.7", {"start": v(-179.44, 2368) * mm, "end": v(-179.44, 2357.53) * mm});
            skLineSegment(sketch, "E26.5.0", {"start": v(-182.14, 2290.39) * mm, "end": v(-175.76, 2298.7) * mm});
            skLineSegment(sketch, "E26.5.1", {"start": v(-161.37, 2287.65) * mm, "end": v(-167.75, 2279.34) * mm});
            skLineSegment(sketch, "E26.5.2", {"start": v(-178.13, 2280.71) * mm, "end": v(-182.14, 2290.39) * mm});
            skLineSegment(sketch, "E26.5.3", {"start": v(-167.75, 2279.34) * mm, "end": v(-178.13, 2280.71) * mm});
            skCircle(sketch, "E26.5.4", {"center": v(-171.75, 2289.02) * mm, "radius": 9.07 * mm, "construction": true});
            skPoint(sketch, "E26.5.5", {"position": v(-163.37, 2292.5) * mm});
            skLineSegment(sketch, "E26.5.6", {"start": v(-175.76, 2298.7) * mm, "end": v(-165.38, 2297.33) * mm});
            skLineSegment(sketch, "E26.5.7", {"start": v(-165.38, 2297.33) * mm, "end": v(-161.37, 2287.65) * mm});
            skLineSegment(sketch, "E26.6.0", {"start": v(-138.17, 2224.59) * mm, "end": v(-135.46, 2234.7) * mm});
            skLineSegment(sketch, "E26.6.1", {"start": v(-117.94, 2230.01) * mm, "end": v(-120.65, 2219.9) * mm});
            skLineSegment(sketch, "E26.6.2", {"start": v(-130.77, 2217.18) * mm, "end": v(-138.17, 2224.59) * mm});
            skLineSegment(sketch, "E26.6.3", {"start": v(-120.65, 2219.9) * mm, "end": v(-130.77, 2217.18) * mm});
            skCircle(sketch, "E26.6.4", {"center": v(-128.06, 2227.3) * mm, "radius": 9.07 * mm, "construction": true});
            skPoint(sketch, "E26.6.5", {"position": v(-121.64, 2233.71) * mm});
            skLineSegment(sketch, "E26.6.6", {"start": v(-135.46, 2234.7) * mm, "end": v(-125.35, 2237.42) * mm});
            skLineSegment(sketch, "E26.6.7", {"start": v(-125.35, 2237.42) * mm, "end": v(-117.94, 2230.01) * mm});
            skLineSegment(sketch, "E26.7.0", {"start": v(-72.38, 2180.63) * mm, "end": v(-73.74, 2191) * mm});
            skLineSegment(sketch, "E26.7.1", {"start": v(-55.76, 2193.38) * mm, "end": v(-54.4, 2183) * mm});
            skLineSegment(sketch, "E26.7.2", {"start": v(-62.7, 2176.62) * mm, "end": v(-72.38, 2180.63) * mm});
            skLineSegment(sketch, "E26.7.3", {"start": v(-54.4, 2183) * mm, "end": v(-62.7, 2176.62) * mm});
            skCircle(sketch, "E26.7.4", {"center": v(-64.07, 2187) * mm, "radius": 9.07 * mm, "construction": true});
            skPoint(sketch, "E26.7.5", {"position": v(-60.6, 2195.38) * mm});
            skLineSegment(sketch, "E26.7.6", {"start": v(-73.74, 2191) * mm, "end": v(-65.43, 2197.39) * mm});
            skLineSegment(sketch, "E26.7.7", {"start": v(-65.43, 2197.39) * mm, "end": v(-55.76, 2193.38) * mm});
            skLineSegment(sketch, "E26.8.0", {"start": v(5.24, 2165.19) * mm, "end": v(0, 2174.26) * mm});
            skLineSegment(sketch, "E26.8.1", {"start": v(15.71, 2183.33) * mm, "end": v(20.95, 2174.26) * mm});
            skLineSegment(sketch, "E26.8.2", {"start": v(15.71, 2165.19) * mm, "end": v(5.24, 2165.19) * mm});
            skLineSegment(sketch, "E26.8.3", {"start": v(20.95, 2174.26) * mm, "end": v(15.71, 2165.19) * mm});
            skCircle(sketch, "E26.8.4", {"center": v(10.47, 2174.26) * mm, "radius": 9.07 * mm, "construction": true});
            skPoint(sketch, "E26.8.5", {"position": v(10.47, 2183.33) * mm});
            skLineSegment(sketch, "E26.8.6", {"start": v(0, 2174.26) * mm, "end": v(5.24, 2183.33) * mm});
            skLineSegment(sketch, "E26.8.7", {"start": v(5.24, 2183.33) * mm, "end": v(15.71, 2183.33) * mm});
            skLineSegment(sketch, "E26.9.0", {"start": v(82.85, 2180.63) * mm, "end": v(74.54, 2187) * mm});
            skLineSegment(sketch, "E26.9.1", {"start": v(85.58, 2201.4) * mm, "end": v(93.9, 2195.02) * mm});
            skLineSegment(sketch, "E26.9.2", {"start": v(92.53, 2184.63) * mm, "end": v(82.85, 2180.63) * mm});
            skLineSegment(sketch, "E26.9.3", {"start": v(93.9, 2195.02) * mm, "end": v(92.53, 2184.63) * mm});
            skCircle(sketch, "E26.9.4", {"center": v(84.22, 2191) * mm, "radius": 9.07 * mm, "construction": true});
            skPoint(sketch, "E26.9.5", {"position": v(80.75, 2199.39) * mm});
            skLineSegment(sketch, "E26.9.6", {"start": v(74.54, 2187) * mm, "end": v(75.9, 2197.39) * mm});
            skLineSegment(sketch, "E26.9.7", {"start": v(75.9, 2197.39) * mm, "end": v(85.58, 2201.4) * mm});
            skLineSegment(sketch, "E26.10.0", {"start": v(148.65, 2224.59) * mm, "end": v(138.53, 2227.3) * mm});
            skLineSegment(sketch, "E26.10.1", {"start": v(143.23, 2244.82) * mm, "end": v(153.34, 2242.11) * mm});
            skLineSegment(sketch, "E26.10.2", {"start": v(156.05, 2232) * mm, "end": v(148.65, 2224.59) * mm});
            skLineSegment(sketch, "E26.10.3", {"start": v(153.34, 2242.11) * mm, "end": v(156.05, 2232) * mm});
            skCircle(sketch, "E26.10.4", {"center": v(145.94, 2234.7) * mm, "radius": 9.07 * mm, "construction": true});
            skPoint(sketch, "E26.10.5", {"position": v(139.52, 2241.12) * mm});
            skLineSegment(sketch, "E26.10.6", {"start": v(138.53, 2227.3) * mm, "end": v(135.82, 2237.42) * mm});
            skLineSegment(sketch, "E26.10.7", {"start": v(135.82, 2237.42) * mm, "end": v(143.23, 2244.82) * mm});
            skLineSegment(sketch, "E26.11.0", {"start": v(192.61, 2290.39) * mm, "end": v(182.23, 2289.02) * mm});
            skLineSegment(sketch, "E26.11.1", {"start": v(179.86, 2307) * mm, "end": v(190.24, 2308.37) * mm});
            skLineSegment(sketch, "E26.11.2", {"start": v(196.62, 2300.06) * mm, "end": v(192.61, 2290.39) * mm});
            skLineSegment(sketch, "E26.11.3", {"start": v(190.24, 2308.37) * mm, "end": v(196.62, 2300.06) * mm});
            skCircle(sketch, "E26.11.4", {"center": v(186.24, 2298.7) * mm, "radius": 9.07 * mm, "construction": true});
            skPoint(sketch, "E26.11.5", {"position": v(177.86, 2302.17) * mm});
            skLineSegment(sketch, "E26.11.6", {"start": v(182.23, 2289.02) * mm, "end": v(175.85, 2297.33) * mm});
            skLineSegment(sketch, "E26.11.7", {"start": v(175.85, 2297.33) * mm, "end": v(179.86, 2307) * mm});
            skLineSegment(sketch, "E26.12.0", {"start": v(208.05, 2368) * mm, "end": v(198.98, 2362.76) * mm});
            skLineSegment(sketch, "E26.12.1", {"start": v(189.9, 2378.47) * mm, "end": v(198.98, 2383.71) * mm});
            skLineSegment(sketch, "E26.12.2", {"start": v(208.05, 2378.47) * mm, "end": v(208.05, 2368) * mm});
            skLineSegment(sketch, "E26.12.3", {"start": v(198.98, 2383.71) * mm, "end": v(208.05, 2378.47) * mm});
            skCircle(sketch, "E26.12.4", {"center": v(198.98, 2373.24) * mm, "radius": 9.07 * mm, "construction": true});
            skPoint(sketch, "E26.12.5", {"position": v(189.9, 2373.24) * mm});
            skLineSegment(sketch, "E26.12.6", {"start": v(198.98, 2362.76) * mm, "end": v(189.9, 2368) * mm});
            skLineSegment(sketch, "E26.12.7", {"start": v(189.9, 2368) * mm, "end": v(189.9, 2378.47) * mm});
            skLineSegment(sketch, "E26.13.0", {"start": v(192.61, 2445.61) * mm, "end": v(186.24, 2437.3) * mm});
            skLineSegment(sketch, "E26.13.1", {"start": v(171.84, 2448.35) * mm, "end": v(178.22, 2456.66) * mm});
            skLineSegment(sketch, "E26.13.2", {"start": v(188.6, 2455.29) * mm, "end": v(192.61, 2445.61) * mm});
            skLineSegment(sketch, "E26.13.3", {"start": v(178.22, 2456.66) * mm, "end": v(188.6, 2455.29) * mm});
            skCircle(sketch, "E26.13.4", {"center": v(182.23, 2446.98) * mm, "radius": 9.07 * mm, "construction": true});
            skPoint(sketch, "E26.13.5", {"position": v(173.85, 2443.5) * mm});
            skLineSegment(sketch, "E26.13.6", {"start": v(186.24, 2437.3) * mm, "end": v(175.85, 2438.67) * mm});
            skLineSegment(sketch, "E26.13.7", {"start": v(175.85, 2438.67) * mm, "end": v(171.84, 2448.35) * mm});
            skLineSegment(sketch, "E26.14.0", {"start": v(148.65, 2511.41) * mm, "end": v(145.94, 2501.3) * mm});
            skLineSegment(sketch, "E26.14.1", {"start": v(128.41, 2505.99) * mm, "end": v(131.12, 2516.1) * mm});
            skLineSegment(sketch, "E26.14.2", {"start": v(141.24, 2518.82) * mm, "end": v(148.65, 2511.41) * mm});
            skLineSegment(sketch, "E26.14.3", {"start": v(131.12, 2516.1) * mm, "end": v(141.24, 2518.82) * mm});
            skCircle(sketch, "E26.14.4", {"center": v(138.53, 2508.7) * mm, "radius": 9.07 * mm, "construction": true});
            skPoint(sketch, "E26.14.5", {"position": v(132.12, 2502.29) * mm});
            skLineSegment(sketch, "E26.14.6", {"start": v(145.94, 2501.3) * mm, "end": v(135.82, 2498.58) * mm});
            skLineSegment(sketch, "E26.14.7", {"start": v(135.82, 2498.58) * mm, "end": v(128.41, 2505.99) * mm});
            skLineSegment(sketch, "E26.15.0", {"start": v(82.85, 2555.37) * mm, "end": v(84.22, 2545) * mm});
            skLineSegment(sketch, "E26.15.1", {"start": v(66.23, 2542.62) * mm, "end": v(64.86, 2553) * mm});
            skLineSegment(sketch, "E26.15.2", {"start": v(73.17, 2559.38) * mm, "end": v(82.85, 2555.37) * mm});
            skLineSegment(sketch, "E26.15.3", {"start": v(64.86, 2553) * mm, "end": v(73.17, 2559.38) * mm});
            skCircle(sketch, "E26.15.4", {"center": v(74.54, 2549) * mm, "radius": 9.07 * mm, "construction": true});
            skPoint(sketch, "E26.15.5", {"position": v(71.07, 2540.62) * mm});
            skLineSegment(sketch, "E26.15.6", {"start": v(84.22, 2545) * mm, "end": v(75.9, 2538.61) * mm});
            skLineSegment(sketch, "E26.15.7", {"start": v(75.9, 2538.61) * mm, "end": v(66.23, 2542.62) * mm});
            skPoint(sketch, "E26.center", {"position": v(5.24, 2368) * mm});
            skSolve(sketch);
        }
        {
            var Q0;
            Q0 = qSketchRegion(id + "F23", true);
            extrude(context, id + "F24", {"entities" : qUnion([Q0]), "operationType" : NewBodyOperationType.ADD, "depth" : 10 * mm, "offsetDistance" : 25 * mm, "hasSecondDirection" : true, "secondDirectionOppositeDirection" : true, "secondDirectionDepth" : 50 * mm});
        }
        {
            var Q0;
            Q0=qCreatedBy(id+"F2.planeOp",FACE);
            cPlane(context, id + "F25", {"entities" : qUnion([Q0]), "cplaneType" : CPlaneType.OFFSET, "offset" : 2800 * mm, "width" : 150 * mm, "height" : 150 * mm});
        }
        {
            var Q0;
            Q0=qCreatedBy(id+"F25.planeOp",FACE);
            var sketch = newSketch(context, id + "F26", { "sketchPlane" : qUnion([Q0])});
            skCircle(sketch, "E27", {"center": v(0, 0) * mm, "radius": 15 * mm});
            skCircle(sketch, "E28", {"center": v(0, 0) * mm, "radius": 10 * mm});
            skSolve(sketch);
        }
        {
            var Q0;
            Q0 = qSketchRegion(id + "F26", true);
            extrude(context, id + "F27", {"entities" : qUnion([Q0]), "operationType" : NewBodyOperationType.ADD, "depth" : 300 * mm, "offsetDistance" : 25 * mm});
        }
        {
            var Q0;
            Q0=makeQuery(id+"F27.opExtrude","CAP_FACE",FACE,{"disambiguationData":[OSD([sQuery(id+"F26.wireOp",EDGE,"E27"),sQuery(id+"F26.wireOp",EDGE,"E28")])],"isStart":false});
            var sketch = newSketch(context, id + "F28", { "sketchPlane" : qUnion([Q0])});
            skCircle(sketch, "E29", {"center": v(0, 0) * mm, "radius": 52.5 * mm});
            skCircle(sketch, "E30", {"center": v(37.5, 0) * mm, "radius": 5.5 * mm});
            skCircle(sketch, "E31.1.0", {"center": v(0, 37.5) * mm, "radius": 5.5 * mm});
            skCircle(sketch, "E31.2.0", {"center": v(-37.5, 0) * mm, "radius": 5.5 * mm});
            skCircle(sketch, "E31.3.0", {"center": v(0, -37.5) * mm, "radius": 5.5 * mm});
            skSolve(sketch);
        }
        {
            var Q0;
            Q0=makeQuery(id+"F28.imprint","IMPRINT",FACE,{"disambiguationData":[TD([[makeQuery(id+"F28.imprint","IMPRINT",EDGE,{"derivedFrom":sQuery(id+"F28.wireOp",EDGE,"E29")}),1.0]])]});
            extrude(context, id + "F29", {"entities" : qUnion([Q0]), "operationType" : NewBodyOperationType.ADD, "oppositeDirection" : true, "depth" : 10 * mm, "offsetDistance" : 25 * mm});
        }
        {
            var Q0;
            Q0=qCreatedBy(id+"F14.planeOp",FACE);
            var sketch = newSketch(context, id + "F30", { "sketchPlane" : qUnion([Q0])});
            skCircle(sketch, "E32", {"center": v(0, 633.05) * mm, "radius": 67.5 * mm});
            skCircle(sketch, "E33", {"center": v(0, 633.05) * mm, "radius": 62.5 * mm});
            skSolve(sketch);
        }
        {
            var Q0;
            Q0 = qSketchRegion(id + "F30", true);
            extrude(context, id + "F31", {"entities" : qUnion([Q0]), "operationType" : NewBodyOperationType.ADD, "depth" : 700 * mm, "offsetDistance" : 25 * mm});
        }
        {
            var Q0;
            Q0=makeQuery(id+"F31.opExtrude","CAP_FACE",FACE,{"disambiguationData":[OSD([sQuery(id+"F30.wireOp",EDGE,"E32"),sQuery(id+"F30.wireOp",EDGE,"E33")])],"isStart":false});
            var sketch = newSketch(context, id + "F32", { "sketchPlane" : qUnion([Q0])});
            skCircle(sketch, "E34", {"center": v(0, 633.05) * mm, "radius": 125 * mm});
            skCircle(sketch, "E35", {"center": v(0, 738.05) * mm, "radius": 11 * mm});
            skCircle(sketch, "E36.1.0", {"center": v(-74.25, 707.3) * mm, "radius": 11 * mm});
            skCircle(sketch, "E36.2.0", {"center": v(-105, 633.05) * mm, "radius": 11 * mm});
            skCircle(sketch, "E36.3.0", {"center": v(-74.25, 558.8) * mm, "radius": 11 * mm});
            skCircle(sketch, "E36.4.0", {"center": v(0, 528.05) * mm, "radius": 11 * mm});
            skCircle(sketch, "E36.5.0", {"center": v(74.25, 558.8) * mm, "radius": 11 * mm});
            skCircle(sketch, "E36.6.0", {"center": v(105, 633.05) * mm, "radius": 11 * mm});
            skCircle(sketch, "E36.7.0", {"center": v(74.25, 707.3) * mm, "radius": 11 * mm});
            skSolve(sketch);
        }
        {
            var Q0;
            Q0=makeQuery(id+"F32.imprint","IMPRINT",FACE,{"disambiguationData":[TD([[makeQuery(id+"F32.imprint","IMPRINT",EDGE,{"derivedFrom":sQuery(id+"F32.wireOp",EDGE,"E34")}),1.0]])]});
            extrude(context, id + "F33", {"entities" : qUnion([Q0]), "operationType" : NewBodyOperationType.ADD, "oppositeDirection" : true, "depth" : 15 * mm, "offsetDistance" : 25 * mm});
        }
    });
